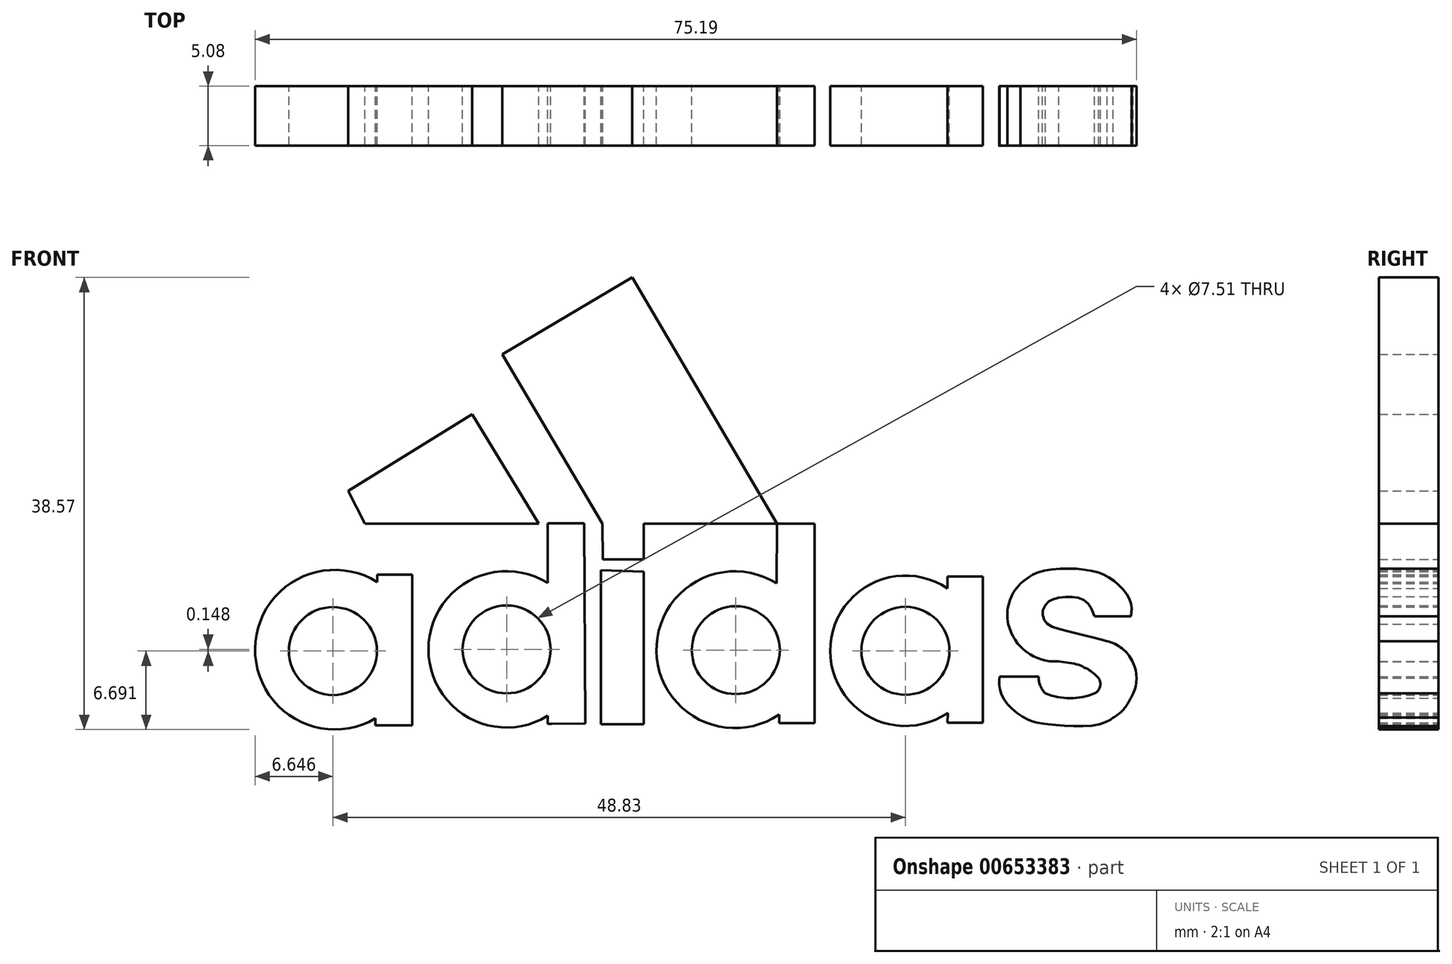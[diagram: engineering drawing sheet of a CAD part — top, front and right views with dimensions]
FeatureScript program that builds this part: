
annotation { "Feature Type Name" : "Feature", "Feature Type Description" : "" }
export const myFeature = defineFeature(function(context is Context, id is Id, definition is map)
    precondition{}
    {
        {
            var Q0;
            Q0=qCreatedBy(makeId("Front.planeOp"),FACE);
            var sketch = newSketch(context, id + "F0", { "sketchPlane" : qUnion([Q0])});
            skLineSegment(sketch, "E0", {"start": v(-46, -6.55) * mm, "end": v(-44.57, -9.33) * mm});
            skLineSegment(sketch, "E1", {"start": v(-44.57, -9.33) * mm, "end": v(-29.73, -9.33) * mm});
            skLineSegment(sketch, "E2", {"start": v(-46, -6.55) * mm, "end": v(-35.42, 0) * mm});
            skLineSegment(sketch, "E3", {"start": v(-35.42, 0) * mm, "end": v(-29.73, -9.33) * mm});
            skLineSegment(sketch, "E4", {"start": v(-32.85, 5.11) * mm, "end": v(-24.3, -9.33) * mm});
            skLineSegment(sketch, "E5", {"start": v(-24.3, -9.33) * mm, "end": v(-9.43, -9.33) * mm});
            skLineSegment(sketch, "E6", {"start": v(-32.85, 5.11) * mm, "end": v(-21.77, 11.68) * mm});
            skLineSegment(sketch, "E7", {"start": v(-21.77, 11.68) * mm, "end": v(-9.43, -9.33) * mm});
            skLineSegment(sketch, "E8", {"start": v(-19.59, 16.77) * mm, "end": v(-4.19, -9.33) * mm});
            skLineSegment(sketch, "E9", {"start": v(-4.19, -9.33) * mm, "end": v(10.68, -9.33) * mm});
            skLineSegment(sketch, "E10", {"start": v(-19.59, 16.77) * mm, "end": v(-8.73, 23.18) * mm});
            skCircle(sketch, "E11", {"center": v(-47.3, -20.2) * mm, "radius": 3.75 * mm});
            skCircle(sketch, "E12", {"center": v(-32.48, -20.05) * mm, "radius": 3.75 * mm});
            skCircle(sketch, "E13", {"center": v(-12.93, -20.12) * mm, "radius": 3.75 * mm});
            skCircle(sketch, "E14", {"center": v(1.54, -20.18) * mm, "radius": 3.75 * mm});
            skLineSegment(sketch, "E15", {"start": v(-43.5, -14.31) * mm, "end": v(-43.5, -13.66) * mm});
            skLineSegment(sketch, "E16", {"start": v(-43.5, -13.66) * mm, "end": v(-40.54, -13.66) * mm});
            skLineSegment(sketch, "E17", {"start": v(-40.54, -13.66) * mm, "end": v(-40.54, -26.54) * mm});
            skLineSegment(sketch, "E18", {"start": v(-40.54, -26.54) * mm, "end": v(-43.68, -26.54) * mm});
            skLineSegment(sketch, "E19", {"start": v(-43.68, -26.54) * mm, "end": v(-43.68, -25.95) * mm});
            skArc(sketch, "E20", {"start": v(-43.5, -14.31) * mm, "mid": v(-53.94, -19.98) * mm, "end": v(-43.68, -25.95) * mm});
            skArc(sketch, "E21", {"start": v(-28.97, -14.38) * mm, "mid": v(-39.15, -20.05) * mm, "end": v(-28.97, -25.73) * mm});
            skLineSegment(sketch, "E22", {"start": v(-28.97, -14.38) * mm, "end": v(-28.97, -9.3) * mm});
            skLineSegment(sketch, "E23", {"start": v(-28.97, -9.3) * mm, "end": v(-25.86, -9.3) * mm});
            skLineSegment(sketch, "E24", {"start": v(-25.86, -9.3) * mm, "end": v(-25.78, -26.39) * mm});
            skLineSegment(sketch, "E25", {"start": v(-25.78, -26.39) * mm, "end": v(-28.67, -26.4) * mm});
            skLineSegment(sketch, "E26", {"start": v(-28.67, -26.4) * mm, "end": v(-28.97, -26.4) * mm});
            skLineSegment(sketch, "E27", {"start": v(-28.97, -25.73) * mm, "end": v(-28.97, -26.4) * mm});
            skLineSegment(sketch, "E28", {"start": v(-24.43, -13.29) * mm, "end": v(-24.43, -26.45) * mm});
            skLineSegment(sketch, "E29", {"start": v(-24.43, -26.45) * mm, "end": v(-20.8, -26.45) * mm});
            skLineSegment(sketch, "E30", {"start": v(-20.8, -26.45) * mm, "end": v(-20.8, -13.44) * mm});
            skLineSegment(sketch, "E31", {"start": v(-24.43, -13.29) * mm, "end": v(-20.8, -13.44) * mm});
            skLineSegment(sketch, "E32", {"start": v(-24.27, -12.38) * mm, "end": v(-20.8, -12.38) * mm});
            skLineSegment(sketch, "E33", {"start": v(-20.8, -12.38) * mm, "end": v(-20.8, -9.33) * mm});
            skLineSegment(sketch, "E34", {"start": v(-24.27, -12.38) * mm, "end": v(-24.3, -9.33) * mm});
            skArc(sketch, "E35", {"start": v(-9.45, -14.42) * mm, "mid": v(-19.7, -20.21) * mm, "end": v(-9.24, -25.6) * mm});
            skLineSegment(sketch, "E36", {"start": v(-9.43, -9.33) * mm, "end": v(-9.45, -14.42) * mm});
            skLineSegment(sketch, "E37", {"start": v(-9.43, -9.33) * mm, "end": v(-6.2, -9.34) * mm});
            skLineSegment(sketch, "E38", {"start": v(-6.2, -9.34) * mm, "end": v(-6.2, -26.35) * mm});
            skLineSegment(sketch, "E39", {"start": v(-6.2, -26.35) * mm, "end": v(-9.24, -26.35) * mm});
            skLineSegment(sketch, "E40", {"start": v(-9.24, -25.6) * mm, "end": v(-9.24, -26.35) * mm});
            skArc(sketch, "E41", {"start": v(11.34, -14.45) * mm, "mid": v(10.39, -16.05) * mm, "end": v(10.31, -17.9) * mm});
            skArc(sketch, "E42", {"start": v(10.31, -17.9) * mm, "mid": v(11.88, -20.28) * mm, "end": v(14.62, -21.08) * mm});
            skArc(sketch, "E43", {"start": v(20.97, -23.82) * mm, "mid": v(20.9, -21.06) * mm, "end": v(18.73, -19.36) * mm});
            skLineSegment(sketch, "E44", {"start": v(17.67, -17.22) * mm, "end": v(20.76, -17.22) * mm});
            skLineSegment(sketch, "E45", {"start": v(12.89, -22.37) * mm, "end": v(9.57, -22.37) * mm});
            skArc(sketch, "E46", {"start": v(12.89, -22.37) * mm, "mid": v(13.04, -23.15) * mm, "end": v(13.49, -23.82) * mm});
            skArc(sketch, "E47", {"start": v(13.49, -23.82) * mm, "mid": v(15.58, -24.23) * mm, "end": v(17.67, -23.82) * mm});
            skArc(sketch, "E48", {"start": v(17.67, -23.82) * mm, "mid": v(18.14, -23.24) * mm, "end": v(18, -22.52) * mm});
            skFitSpline(sketch, "E49", {"points": [v(20.76, -17.22) * mm, v(20.76, -16.05) * mm, v(19.4, -14.26) * mm, v(17, -13.28) * mm, v(12.93, -13.46) * mm, v(11.34, -14.45) * mm], "startDerivative": vector(0.95, 7.63) * mm, "endDerivative": vector(-7.28, -6.38) * mm});
            skFitSpline(sketch, "E50", {"points": [v(18.73, -19.36) * mm, v(17.37, -19) * mm, v(15.22, -18.46) * mm, v(13.74, -17.97) * mm, v(13.35, -17.47) * mm, v(13.22, -16.8) * mm, v(13.65, -16.08) * mm, v(14.05, -15.8) * mm, v(15.26, -15.57) * mm, v(16.34, -15.68) * mm, v(17.13, -16.15) * mm, v(17.51, -16.83) * mm, v(17.67, -17.22) * mm], "startDerivative": vector(-12.6, 3.48) * mm, "endDerivative": vector(2.85, -6.39) * mm});
            skFitSpline(sketch, "E51", {"points": [v(14.62, -21.08) * mm, v(16, -21.29) * mm, v(16.81, -21.6) * mm, v(17.27, -21.85) * mm, v(17.68, -22.18) * mm, v(18, -22.52) * mm], "startDerivative": vector(4.2, -0.67) * mm, "endDerivative": vector(1.9, -2.57) * mm});
            skFitSpline(sketch, "E52", {"points": [v(9.57, -22.37) * mm, v(9.57, -23.4) * mm, v(10.38, -24.9) * mm, v(12.25, -26.16) * mm, v(13.62, -26.43) * mm, v(17.77, -26.5) * mm, v(19.26, -25.88) * mm], "startDerivative": vector(-0.81, -7.69) * mm, "endDerivative": vector(3.89, 3.78) * mm});
            skFitSpline(sketch, "E53", {"points": [v(19.26, -25.88) * mm, v(20.13, -25.18) * mm, v(20.97, -23.82) * mm], "startDerivative": vector(2, 1.32) * mm, "endDerivative": vector(1.44, 2.77) * mm});
            skFitSpline(sketch, "E54", {"points": [v(21.03, -23.82) * mm, v(20.97, -23.82) * mm], "startDerivative": vector(-0.05, 0) * mm, "endDerivative": vector(-0.05, 0) * mm});
            skArc(sketch, "E55", {"start": v(5.12, -14.85) * mm, "mid": v(-4.88, -20.2) * mm, "end": v(5.15, -25.48) * mm});
            skLineSegment(sketch, "E56", {"start": v(5.12, -14.85) * mm, "end": v(5.12, -14.4) * mm});
            skLineSegment(sketch, "E57", {"start": v(5.12, -14.4) * mm, "end": v(5.12, -13.85) * mm});
            skLineSegment(sketch, "E58", {"start": v(5.12, -13.85) * mm, "end": v(8.15, -13.85) * mm});
            skLineSegment(sketch, "E59", {"start": v(8.15, -13.85) * mm, "end": v(8.15, -26.3) * mm});
            skLineSegment(sketch, "E60", {"start": v(8.15, -26.3) * mm, "end": v(5.12, -26.3) * mm});
            skLineSegment(sketch, "E61", {"start": v(5.12, -26.3) * mm, "end": v(5.15, -25.48) * mm});
            skLineSegment(sketch, "E62", {"start": v(-8.73, 23.18) * mm, "end": v(10.68, -9.33) * mm});
            skSolve(sketch);
        }
        {
            var Q0;
            Q0=makeQuery(id+"F0.imprint","IMPRINT",FACE,{"disambiguationData":[TD([[makeQuery(id+"F0.imprint","IMPRINT",EDGE,{"derivedFrom":sQuery(id+"F0.wireOp",EDGE,"E0")}),1.0]])]});
            var Q1;
            Q1=makeQuery(id+"F0.imprint","IMPRINT",FACE,{"disambiguationData":[TD([[makeQuery(id+"F0.imprint","IMPRINT",EDGE,{"derivedFrom":sQuery(id+"F0.wireOp",EDGE,"E28")}),1.0]])]});
            var Q2;
            Q2=makeQuery(id+"F0.imprint","IMPRINT",FACE,{"disambiguationData":[TD([[makeQuery(id+"F0.imprint","IMPRINT",EDGE,{"derivedFrom":sQuery(id+"F0.wireOp",EDGE,"E41")}),1.0]])]});
            var Q3;
            {var subQ3=sQuery(id+"F0.wireOp",EDGE,"E4");Q3=makeQuery(id+"F0.imprint","IMPRINT",FACE,{"disambiguationData":[TD([[makeQuery(id+"F0.imprint","IMPRINT",EDGE,{"derivedFrom":subQ3}),1.0]])]});}
            var Q4;
            Q4=makeQuery(id+"F0.imprint","IMPRINT",FACE,{"disambiguationData":[TD([[makeQuery(id+"F0.imprint","IMPRINT",EDGE,{"derivedFrom":sQuery(id+"F0.wireOp",EDGE,"E32")}),1.0]])]});
            var Q5;
            Q5=makeQuery(id+"F0.imprint","IMPRINT",FACE,{"disambiguationData":[TD([[makeQuery(id+"F0.imprint","IMPRINT",EDGE,{"derivedFrom":sQuery(id+"F0.wireOp",EDGE,"E11")}),-1.0]])]});
            var Q6;
            Q6=makeQuery(id+"F0.imprint","IMPRINT",FACE,{"disambiguationData":[TD([[makeQuery(id+"F0.imprint","IMPRINT",EDGE,{"derivedFrom":sQuery(id+"F0.wireOp",EDGE,"E12")}),-1.0]])]});
            var Q7;
            Q7=makeQuery(id+"F0.imprint","IMPRINT",FACE,{"disambiguationData":[TD([[makeQuery(id+"F0.imprint","IMPRINT",EDGE,{"derivedFrom":sQuery(id+"F0.wireOp",EDGE,"E13")}),-1.0]])]});
            var Q8;
            Q8=makeQuery(id+"F0.imprint","IMPRINT",FACE,{"disambiguationData":[TD([[makeQuery(id+"F0.imprint","IMPRINT",EDGE,{"derivedFrom":sQuery(id+"F0.wireOp",EDGE,"E14")}),-1.0]])]});
            extrude(context, id + "F1", {"entities" : qUnion([Q0, Q1, Q2, Q3, Q4, Q5, Q6, Q7, Q8]), "depth" : 5.08 * mm, "offsetDistance" : 25.4 * mm});
        }
    });
